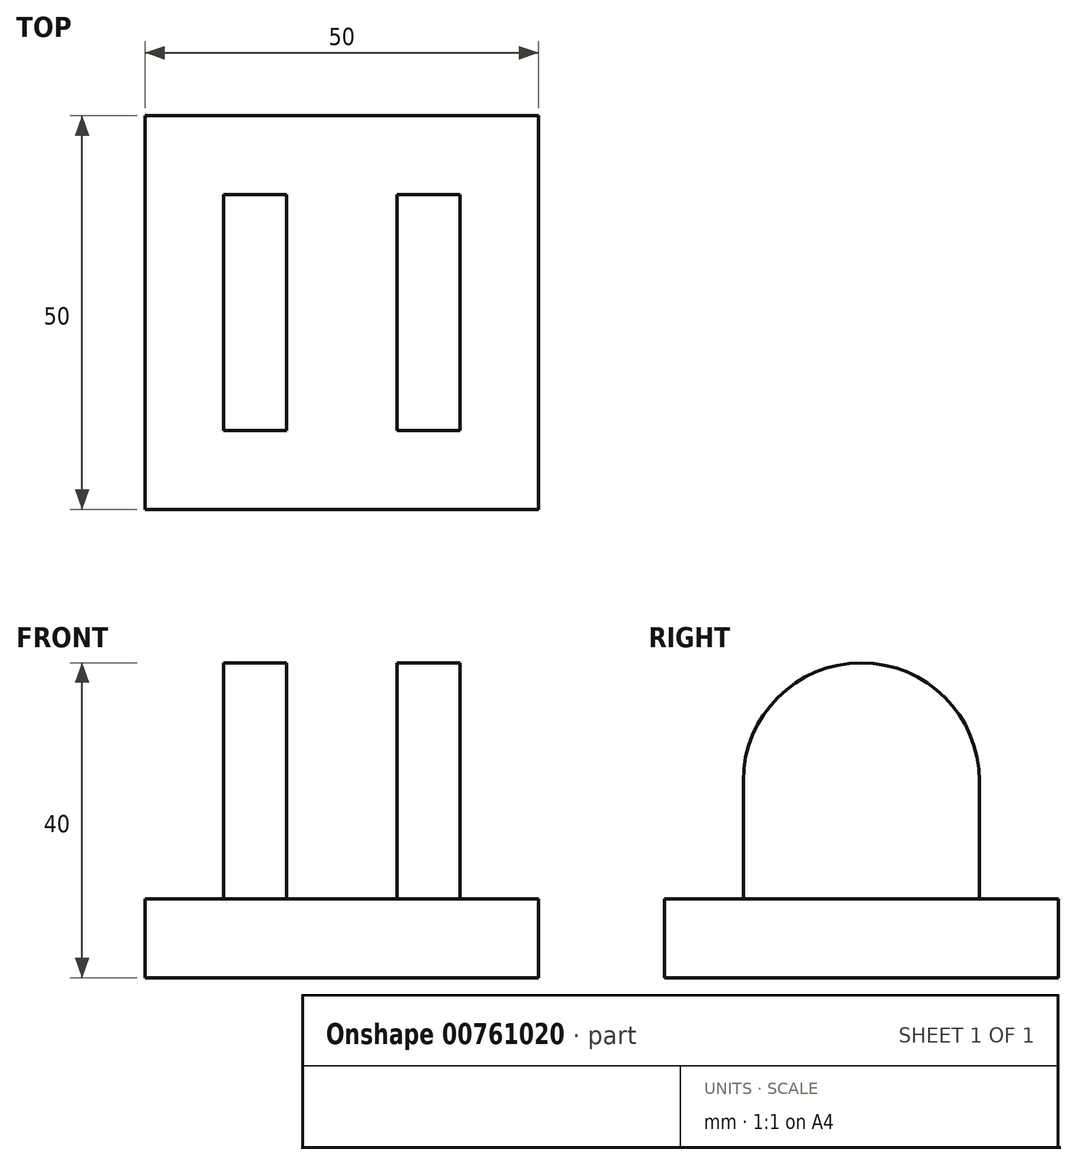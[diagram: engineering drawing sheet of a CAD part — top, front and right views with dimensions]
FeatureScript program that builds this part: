
annotation { "Feature Type Name" : "Feature", "Feature Type Description" : "" }
export const myFeature = defineFeature(function(context is Context, id is Id, definition is map)
    precondition{}
    {
        {
            var Q0;
            Q0=qCreatedBy(makeId("Top.planeOp"),FACE);
            var sketch = newSketch(context, id + "F0", { "sketchPlane" : qUnion([Q0])});
            skLineSegment(sketch, "E0.bottom", {"start": v(-25.77, 12.54) * mm, "end": v(24.23, 12.54) * mm});
            skLineSegment(sketch, "E0.top", {"start": v(-25.77, -37.46) * mm, "end": v(24.23, -37.46) * mm});
            skLineSegment(sketch, "E0.left", {"start": v(-25.77, 12.54) * mm, "end": v(-25.77, -37.46) * mm});
            skLineSegment(sketch, "E0.right", {"start": v(24.23, 12.54) * mm, "end": v(24.23, -37.46) * mm});
            skSolve(sketch);
        }
        {
            var Q0;
            Q0=makeQuery(id+"F0.imprint","IMPRINT",FACE,{"disambiguationData":[TD([[makeQuery(id+"F0.imprint","IMPRINT",EDGE,{"derivedFrom":sQuery(id+"F0.wireOp",EDGE,"E0.bottom")}),-1.0]])]});
            var sketch = newSketch(context, id + "F1", { "sketchPlane" : qUnion([Q0])});
            skLineSegment(sketch, "E1.bottom", {"start": v(-15.77, 2.54) * mm, "end": v(-7.77, 2.54) * mm});
            skLineSegment(sketch, "E1.top", {"start": v(-15.77, -27.46) * mm, "end": v(-7.77, -27.46) * mm});
            skLineSegment(sketch, "E1.left", {"start": v(-15.77, 2.54) * mm, "end": v(-15.77, -27.46) * mm});
            skLineSegment(sketch, "E1.right", {"start": v(-7.77, 2.54) * mm, "end": v(-7.77, -27.46) * mm});
            skSolve(sketch);
        }
        {
            var Q0;
            Q0=makeQuery(id+"F0.imprint","IMPRINT",FACE,{"disambiguationData":[TD([[makeQuery(id+"F0.imprint","IMPRINT",EDGE,{"derivedFrom":sQuery(id+"F0.wireOp",EDGE,"E0.bottom")}),-1.0]])]});
            var sketch = newSketch(context, id + "F2", { "sketchPlane" : qUnion([Q0])});
            skLineSegment(sketch, "E2.bottom", {"start": v(6.23, 2.54) * mm, "end": v(14.23, 2.54) * mm});
            skLineSegment(sketch, "E2.top", {"start": v(6.23, -27.46) * mm, "end": v(14.23, -27.46) * mm});
            skLineSegment(sketch, "E2.left", {"start": v(6.23, 2.54) * mm, "end": v(6.23, -27.46) * mm});
            skLineSegment(sketch, "E2.right", {"start": v(14.23, 2.54) * mm, "end": v(14.23, -27.46) * mm});
            skSolve(sketch);
        }
        {
            var Q0;
            Q0 = qSketchRegion(id + "F0", true);
            extrude(context, id + "F3", {"entities" : qUnion([Q0]), "depth" : 10 * mm, "offsetDistance" : 25 * mm});
        }
        {
            var Q0;
            Q0=makeQuery(id+"F2.imprint","IMPRINT",FACE,{"disambiguationData":[TD([[makeQuery(id+"F2.imprint","IMPRINT",EDGE,{"derivedFrom":sQuery(id+"F2.wireOp",EDGE,"E2.bottom")}),-1.0]])]});
            extrude(context, id + "F4", {"entities" : qUnion([Q0]), "operationType" : NewBodyOperationType.ADD, "depth" : 40 * mm, "offsetDistance" : 25 * mm});
        }
        {
            var Q0;
            Q0 = qSketchRegion(id + "F1", true);
            extrude(context, id + "F5", {"entities" : qUnion([Q0]), "operationType" : NewBodyOperationType.ADD, "depth" : 40 * mm, "offsetDistance" : 25 * mm});
        }
        {
            var Q0;
            Q0=makeQuery(id+"F5.opExtrude","CAP_EDGE",EDGE,{"disambiguationData":[OSD([sQuery(id+"F1.wireOp",EDGE,"E1.top")])],"isStart":false});
            var Q1;
            Q1=makeQuery(id+"F5.opExtrude","CAP_EDGE",EDGE,{"disambiguationData":[OSD([sQuery(id+"F1.wireOp",EDGE,"E1.bottom")])],"isStart":false});
            fillet(context, id + "F6", {"entities" : qUnion([Q0, Q1]), "radius" : 15 * mm, "tangentPropagation" : true, "allowEdgeOverflow" : false});
        }
        {
            var Q0;
            Q0=makeQuery(id+"F4.opExtrude","CAP_EDGE",EDGE,{"disambiguationData":[OSD([sQuery(id+"F2.wireOp",EDGE,"E2.bottom")])],"isStart":false});
            var Q1;
            Q1=makeQuery(id+"F4.opExtrude","CAP_EDGE",EDGE,{"disambiguationData":[OSD([sQuery(id+"F2.wireOp",EDGE,"E2.top")])],"isStart":false});
            fillet(context, id + "F7", {"entities" : qUnion([Q0, Q1]), "radius" : 15 * mm, "tangentPropagation" : true, "allowEdgeOverflow" : false});
        }
    });
